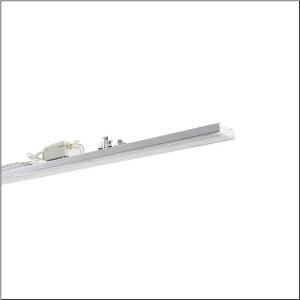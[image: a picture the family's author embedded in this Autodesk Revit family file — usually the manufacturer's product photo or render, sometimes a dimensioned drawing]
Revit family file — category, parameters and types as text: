
# Revit family: licross_21_recessed_mo_52te187n485g
name_source: partatom
category: Lighting Fixtures
units: mm (PartAtom-declared; Revit-internal decimal feet)

## family parameters
Cut with Voids When Loaded = No
Host = Face
Light Source = No
Part Type = Normal
Room Calculation Point = No
Round Connector Dimension = Use Diameter
Shared = No

## types (1)
- Licross 21 Recessed MO (1 x LED, 8570 lm, 47.9 W, 4000K)
    Apparent Load = 48 VA
    CIE Flux Codes = 79 95 99 100 100
    Color Rendering = 80
    Color Temperature = 4000K
    Default Elevation = 1800 mm
    Description = Licross 21 Recessed MO, luminaire insert, of sheet steel, galvanised, coil coated, white, length: 1.500mm, width: 66mm, height: 67mm, LED rated luminous flux: 8.570lm, light colour: 840, SDCM (Standard Deviation of Colour Matching)MacAdam ≤ 3 SDCM (initial), control gear: ON/OFF, with plug, 3-pole, with phase selection, mains connection: 220..240V, AC, 50/60Hz, rated input power: 48W, internal wiring halogen-free, primary light control with lens, of plastic, primary optical cover: cover, of PMMA, light emission: direct distribution, primary light characteristic: symmetric, protection rating (complete): IP54, insulation class (complete): insulation class I (protective earthing), certification: CE, ENEC, VDE, UKCA, protection symbol: D if used in an environment with non-conductive dust loads with corresponding accessories, impact resistance: IK06, permissible ambient temperature for indoor applications: -35..+40°C, corresponds to IFS (International Featured Standards) requirements for safety and quality in the food industry, reducing of maximum allowable ambient temperature of 5°C with ceiling mounting, LABS conformity tested according to VDMA 24364:2018-05, The light source and the operating device comply with the requirements of the Ecodesign Regulation (EU) 2019/2020 and are replaceable in accordance with this regulation, packaging unit: 1 piece
    Height = 58 mm
    Lamp = 1 x LED
    Lamp Light Flux = 8570 lm
    Lamp Power = 47.9 W
    Lamp count = 1
    Length = 1500 mm
    Luminous efficacy = 179 lm/W
    Manufacturer = Siteco
    ModVariant = No
    Model = 52TE187N485G
    Mounting Place = Ceiling
    Mounting Type = Pendant
    Number of Poles = 1
    OnlyDefault = Yes
    Power Factor = 1
    Product Name = Licross 21 Recessed MO
    Product group = luminaire insert | ceiling pendant
    ProductGroupID = 901
    Protection Class = Protection class I
    Protection Degree = IP 54
    RLX_Detail_Level = 1
    RLX_Emergency_Light_Flux = 0 lm
    RLX_Emergency_Type = 0
    RLX_Emergency_Type_DB = No
    RlxData = <blob elided: 21141 chars, md5=d23a5ef9>
    Socket = socket
    Standby Power = 0 W
    System Light Flux = 8570 lm
    System Power = 48 W
    Type Comments = Product without accessories
    Type Image = l_1296930.jpg
    URL = http://relux.com
    VarID = ---
    Voltage = 0 V
    Weight = 0.00 kg
    Width = 66 mm

## geometry (parser evidence)
native form markers: Blend x4, Sweep x12
no freeform markers — native parametric forms only
